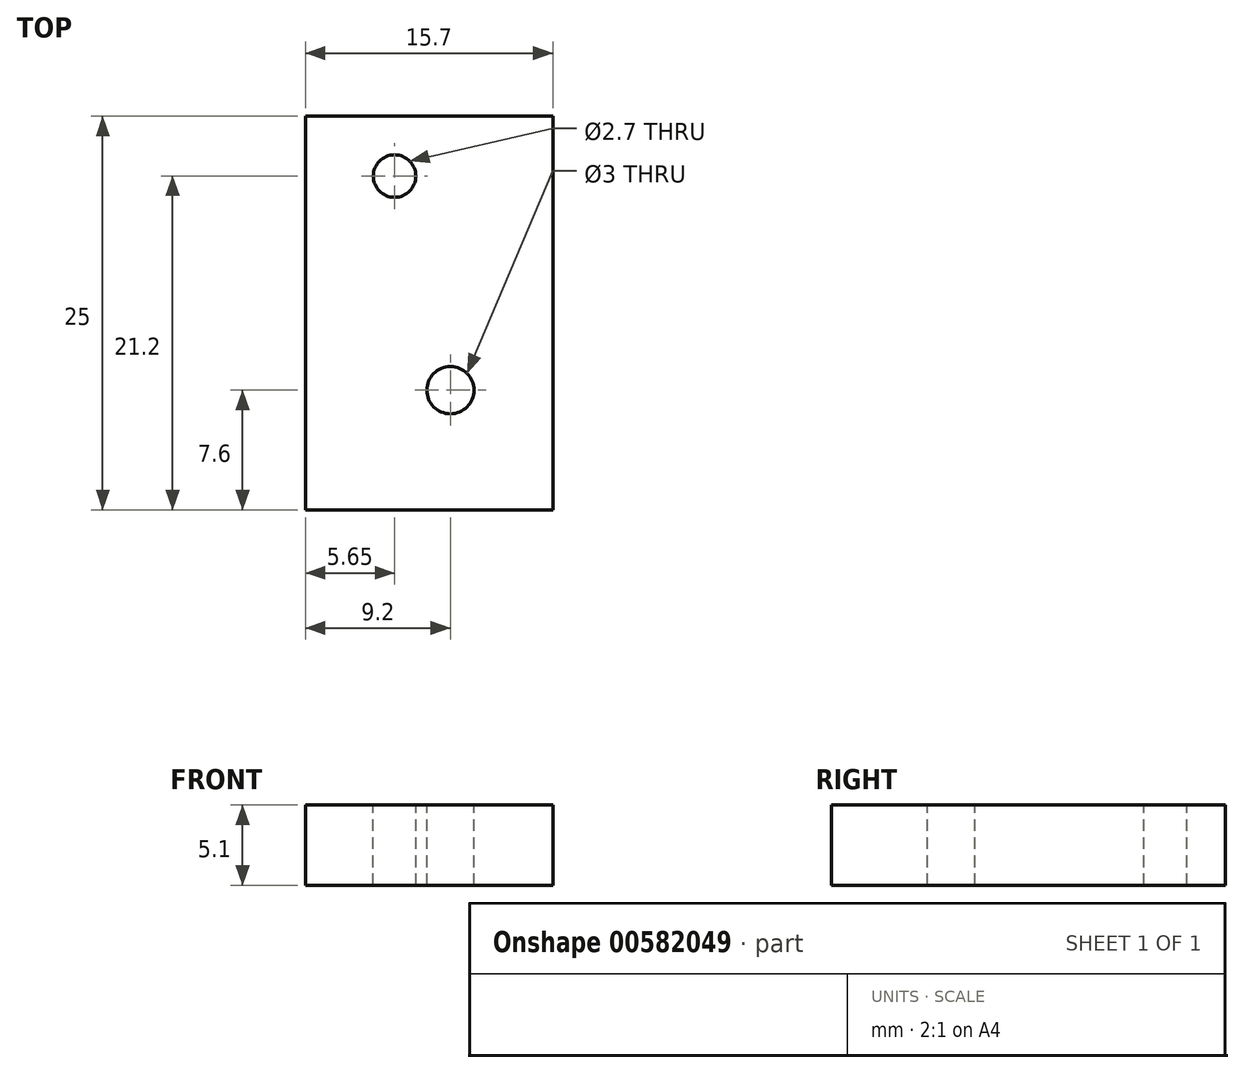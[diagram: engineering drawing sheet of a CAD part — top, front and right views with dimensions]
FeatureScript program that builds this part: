
annotation { "Feature Type Name" : "Feature", "Feature Type Description" : "" }
export const myFeature = defineFeature(function(context is Context, id is Id, definition is map)
    precondition{}
    {
        {
            var Q0;
            Q0=qCreatedBy(makeId("Front.planeOp"),FACE);
            var sketch = newSketch(context, id + "F0", { "sketchPlane" : qUnion([Q0])});
            skLineSegment(sketch, "E0.bottom", {"start": v(-9.54, 5.1) * mm, "end": v(-25.24, 5.1) * mm});
            skLineSegment(sketch, "E0.top", {"start": v(-9.54, 0) * mm, "end": v(-25.24, 0) * mm});
            skLineSegment(sketch, "E0.left", {"start": v(-9.54, 5.1) * mm, "end": v(-9.54, 0) * mm});
            skLineSegment(sketch, "E0.right", {"start": v(-25.24, 5.1) * mm, "end": v(-25.24, 0) * mm});
            skSolve(sketch);
        }
        {
            var Q0;
            Q0 = qSketchRegion(id + "F0", true);
            extrude(context, id + "F1", {"entities" : qUnion([Q0]), "depth" : 25 * mm, "offsetDistance" : 25 * mm});
        }
        {
            var Q0;
            Q0=makeQuery(id+"F1.opExtrude","SWEPT_FACE",FACE,{"disambiguationData":[OSD([sQuery(id+"F0.wireOp",EDGE,"E0.bottom")])]});
            var sketch = newSketch(context, id + "F2", { "sketchPlane" : qUnion([Q0])});
            skCircle(sketch, "E1", {"center": v(-19.59, -3.8) * mm, "radius": 1.35 * mm});
            skSolve(sketch);
        }
        {
            var Q0;
            Q0 = qSketchRegion(id + "F2", true);
            extrude(context, id + "F3", {"entities" : qUnion([Q0]), "operationType" : NewBodyOperationType.REMOVE, "oppositeDirection" : true, "depth" : 5.1 * mm, "offsetDistance" : 25 * mm});
        }
        {
            var Q0;
            Q0=makeQuery(id+"F1.opExtrude","SWEPT_FACE",FACE,{"disambiguationData":[OSD([sQuery(id+"F0.wireOp",EDGE,"E0.bottom")])]});
            var sketch = newSketch(context, id + "F4", { "sketchPlane" : qUnion([Q0])});
            skCircle(sketch, "E2", {"center": v(-16.04, -17.4) * mm, "radius": 1.5 * mm});
            skSolve(sketch);
        }
        {
            var Q0;
            Q0 = qSketchRegion(id + "F4", true);
            extrude(context, id + "F5", {"entities" : qUnion([Q0]), "operationType" : NewBodyOperationType.REMOVE, "oppositeDirection" : true, "depth" : 5.1 * mm, "offsetDistance" : 25 * mm});
        }
    });
